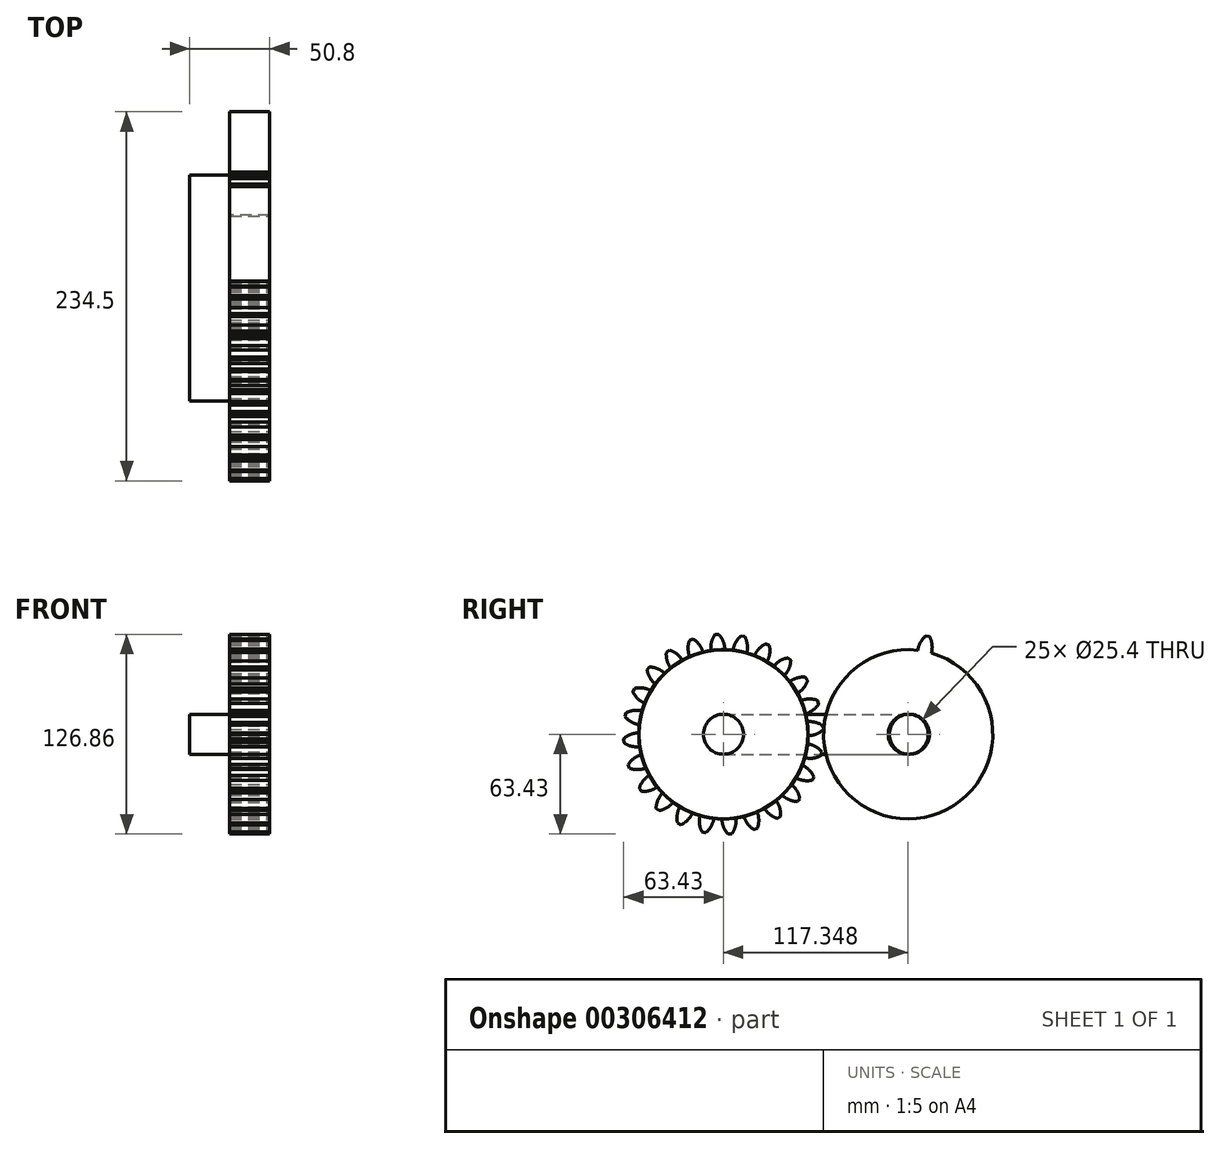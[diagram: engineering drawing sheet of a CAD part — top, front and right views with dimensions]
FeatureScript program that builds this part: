
annotation { "Feature Type Name" : "Feature", "Feature Type Description" : "" }
export const myFeature = defineFeature(function(context is Context, id is Id, definition is map)
    precondition{}
    {
        {
            var Q0;
            Q0=qCreatedBy(makeId("Right.planeOp"),FACE);
            var sketch = newSketch(context, id + "F0", { "sketchPlane" : qUnion([Q0])});
            skLineSegment(sketch, "E0.bottom", {"start": v(0, 0) * mm, "end": v(118.11, 0) * mm});
            skLineSegment(sketch, "E0.top", {"start": v(0, 25.4) * mm, "end": v(118.11, 25.4) * mm});
            skLineSegment(sketch, "E0.left", {"start": v(0, 0) * mm, "end": v(0, 25.4) * mm});
            skLineSegment(sketch, "E0.right", {"start": v(118.11, 0) * mm, "end": v(118.11, 25.4) * mm});
            skCircle(sketch, "E1", {"center": v(0, 12.7) * mm, "radius": 12.7 * mm});
            skCircle(sketch, "E2", {"center": v(118.11, 12.7) * mm, "radius": 12.7 * mm});
            skSolve(sketch);
        }
        {
            var Q0;
            Q0 = qSketchRegion(id + "F0", true);
            extrude(context, id + "F1", {"entities" : qUnion([Q0]), "depth" : 25.4 * mm});
        }
        {
            var Q0;
            {var subQ0=sQuery(id+"F0.wireOp",EDGE,"E0.left");Q0=makeQuery(id+"F0.imprint","IMPRINT",FACE,{"disambiguationData":[TD([[makeQuery(id+"F0.imprint","IMPRINT",EDGE,{"derivedFrom":subQ0}),1.0]])]});}
            var Q1;
            {var subQ0=sQuery(id+"F0.wireOp",EDGE,"E0.left");Q1=makeQuery(id+"F0.imprint","IMPRINT",FACE,{"disambiguationData":[TD([[makeQuery(id+"F0.imprint","IMPRINT",EDGE,{"derivedFrom":subQ0}),-1.0]])]});}
            var Q2;
            {var subQ0=sQuery(id+"F0.wireOp",EDGE,"E0.right");Q2=makeQuery(id+"F0.imprint","IMPRINT",FACE,{"disambiguationData":[TD([[makeQuery(id+"F0.imprint","IMPRINT",EDGE,{"derivedFrom":subQ0}),1.0]])]});}
            var Q3;
            {var subQ0=sQuery(id+"F0.wireOp",EDGE,"E0.right");Q3=makeQuery(id+"F0.imprint","IMPRINT",FACE,{"disambiguationData":[TD([[makeQuery(id+"F0.imprint","IMPRINT",EDGE,{"derivedFrom":subQ0}),-1.0]])]});}
            extrude(context, id + "F2", {"entities" : qUnion([Q0, Q1, Q2, Q3]), "operationType" : NewBodyOperationType.ADD, "depth" : 50.8 * mm});
        }
        {
            var Q0;
            Q0=makeQuery(id+"F2.opExtrude","CAP_FACE",FACE,{"disambiguationData":[OSD([sQuery(id+"F0.wireOp",EDGE,"E1")])],"isStart":false});
            var sketch = newSketch(context, id + "F3", { "sketchPlane" : qUnion([Q0])});
            skCircle(sketch, "E3", {"center": v(0, 12.7) * mm, "radius": 12.7 * mm});
            skCircle(sketch, "E4", {"center": v(0, 12.7) * mm, "radius": 53.72 * mm});
            skCircle(sketch, "E5", {"center": v(0, 12.7) * mm, "radius": 58.67 * mm, "construction": true});
            skCircle(sketch, "E6", {"center": v(0, 12.7) * mm, "radius": 63.5 * mm, "construction": true});
            skLineSegment(sketch, "E7", {"start": v(0, 12.7) * mm, "end": v(0, 87.03) * mm, "construction": true});
            skLineSegment(sketch, "E8", {"start": v(0, 12.7) * mm, "end": v(-4.94, 88.14) * mm, "construction": true});
            skLineSegment(sketch, "E9", {"start": v(0, 71.37) * mm, "end": v(-87.6, 71.37) * mm, "construction": true});
            skLineSegment(sketch, "E10", {"start": v(0, 71.37) * mm, "end": v(-87.33, 39.59) * mm, "construction": true});
            skCircle(sketch, "E11", {"center": v(0, 12.7) * mm, "radius": 55.14 * mm, "construction": true});
            skCircle(sketch, "E12", {"center": v(0, 71.37) * mm, "radius": 14.6 * mm, "construction": true});
            skCircle(sketch, "E13", {"center": v(-13.62, 66.13) * mm, "radius": 14.6 * mm, "construction": true});
            skArc(sketch, "E14", {"start": v(0, 71.37) * mm, "mid": v(-1.25, 73.9) * mm, "end": v(-2.97, 76.13) * mm});
            skArc(sketch, "E15", {"start": v(0.99, 66.41) * mm, "mid": v(0.68, 68.93) * mm, "end": v(0, 71.37) * mm});
            skArc(sketch, "E16.MirrorCS", {"start": v(-7.66, 70.87) * mm, "mid": v(-6.75, 73.54) * mm, "end": v(-5.33, 75.98) * mm});
            skArc(sketch, "E17.MirrorCS", {"start": v(-7.99, 65.82) * mm, "mid": v(-8.01, 68.36) * mm, "end": v(-7.66, 70.87) * mm});
            skLineSegment(sketch, "E18", {"start": v(-5.33, 75.98) * mm, "end": v(-2.97, 76.13) * mm});
            skSolve(sketch);
        }
        {
            var Q0;
            Q0 = qSketchRegion(id + "F3", true);
            extrude(context, id + "F4", {"entities" : qUnion([Q0]), "oppositeDirection" : true, "depth" : 25.4 * mm});
        }
        {
            var Q0;
            Q0=makeQuery(id+"F4.opExtrude","SWEPT_BODY",BODY,{"disambiguationData":[OSD([sQuery(id+"F3.wireOp",EDGE,"E3"),sQuery(id+"F3.wireOp",EDGE,"E4"),sQuery(id+"F3.wireOp",EDGE,"E14"),sQuery(id+"F3.wireOp",EDGE,"E15"),sQuery(id+"F3.wireOp",EDGE,"E16.MirrorCS"),sQuery(id+"F3.wireOp",EDGE,"E17.MirrorCS"),sQuery(id+"F3.wireOp",EDGE,"E18")])]});
            var Q1;
            Q1=makeQuery(id+"F4.opExtrude","SWEPT_FACE",FACE,{"disambiguationData":[OSD([sQuery(id+"F3.wireOp",EDGE,"E4")])]});
            circularPattern(context, id + "F5", {"entities" : qUnion([Q0]), "axis" : qUnion([Q1]), "angle" : 15 * degree, "instanceCount" : 24});
        }
        {
            var Q0;
            Q0=makeQuery(id+"F5.opPattern","COPY",BODY,{"derivedFrom":makeQuery(id+"F4.opExtrude","SWEPT_BODY",BODY,{"disambiguationData":[OSD([sQuery(id+"F3.wireOp",EDGE,"E3"),sQuery(id+"F3.wireOp",EDGE,"E4"),sQuery(id+"F3.wireOp",EDGE,"E14"),sQuery(id+"F3.wireOp",EDGE,"E15"),sQuery(id+"F3.wireOp",EDGE,"E16.MirrorCS"),sQuery(id+"F3.wireOp",EDGE,"E17.MirrorCS"),sQuery(id+"F3.wireOp",EDGE,"E18")])]}),"instanceName":"23"});
            transform(context, id + "F6", {"entities" : qUnion([Q0]), "transformType" : TransformType.TRANSLATION_3D, "dx" : 0 * mm, "dy" : 117.35 * mm, "dz" : 0 * mm, "makeCopy" : true});
        }
    });
